# Revit family: Gewindestange, DIN 976-1 VA
name_source: partatom
category: HLS-Bauteile
units: mm (PartAtom-declared; Revit-internal decimal feet)

## family parameters
Arbeitsebenenbasiert = Ja
Beim Laden mit Abzugskörper schneiden = Nein
Bemaßung runder Anschluss = Durchmesser verwenden
Beschriftungsausrichtung beibehalten = Nein
Gemeinsam genutzt = Ja
Immer vertikal = Nein
Raumberechnungspunkt = Nein
Teiletyp = Normal

## types (8) — shared parameters
Fabrikat = MEFA
Festigkeitsklasse = 4.6
Länge = 1000 mm  [stored 3.28084 ft]
Material = Edelstahl
Mengeneinheit = St
Vorgabe-Ansicht = 1219 mm

## per-type parameters (varying)
| type | Artikelnummer | D | EAN | Gewicht | Gewinde | Kurztext1 | Kurztext2 | Materialname | vpe |
| Gewindestange DIN976-1 M8x1000 V4A | 0738508 | 7 mm  [stored 0.0229659 ft] | 4250928417053 | 0.33 kg | M8 | Gewindestange DIN 976-1 V4A | M8 x 1.000 mm | V4A | 50 |
| Gewindestange DIN976-1 M10x1000 V2A | 0738009 | 8 mm  [stored 0.0262467 ft] | 4250928417022 | 0.52 kg | M10 | Gewindestange DIN 976-1 V2A | M10 x 1.000 mm | V2A | 25 |
| Gewindestange DIN976-1 M12x1000 V2A | 0738012 | 10 mm  [stored 0.0328084 ft] | 4250928417039 | 0.75 kg | M12 | Gewindestange DIN 976-1 V2A | M12 x 1.000 mm | V2A | 25 |
| Gewindestange DIN976-1 M16x1000 V2A | 0738016 | 14 mm | 4250928417046 | 1.33 kg | M16 | Gewindestange DIN 976-1 V2A | M16 x 1.000 mm | V2A | 10 |
| Gewindestange DIN976-1 M10x1000 V4A | 0738510 | 8 mm  [stored 0.0262467 ft] | 4250928417060 | 0.52 kg | M10 | Gewindestange DIN 976-1 V4A | M10 x 1.000 mm | V4A | 25 |
| Gewindestange DIN976-1 M8x1000 V2A | 0738006 | 7 mm  [stored 0.0229659 ft] | 4250928417015 | 0.33 kg | M8 | Gewindestange DIN 976-1 V2A | M8 x 1.000 mm | V2A | 50 |
| Gewindestange DIN976-1 M12x1000 V4A | 0738512 | 10 mm  [stored 0.0328084 ft] | 4250928417077 | 0.75 kg | M12 | Gewindestange DIN 976-1 V4A | M12 x 1.000 mm | V4A | 25 |
| Gewindestange DIN976-1 M16x1000 V4A | 0738516 | 14 mm | 4250928417084 | 1.33 kg | M16 | Gewindestange DIN 976-1 V4A | M16 x 1.000 mm | V4A | 10 |

note: [stored X ft] marks values corroborated as IEEE doubles in the binary element streams (Revit-internal decimal feet)
